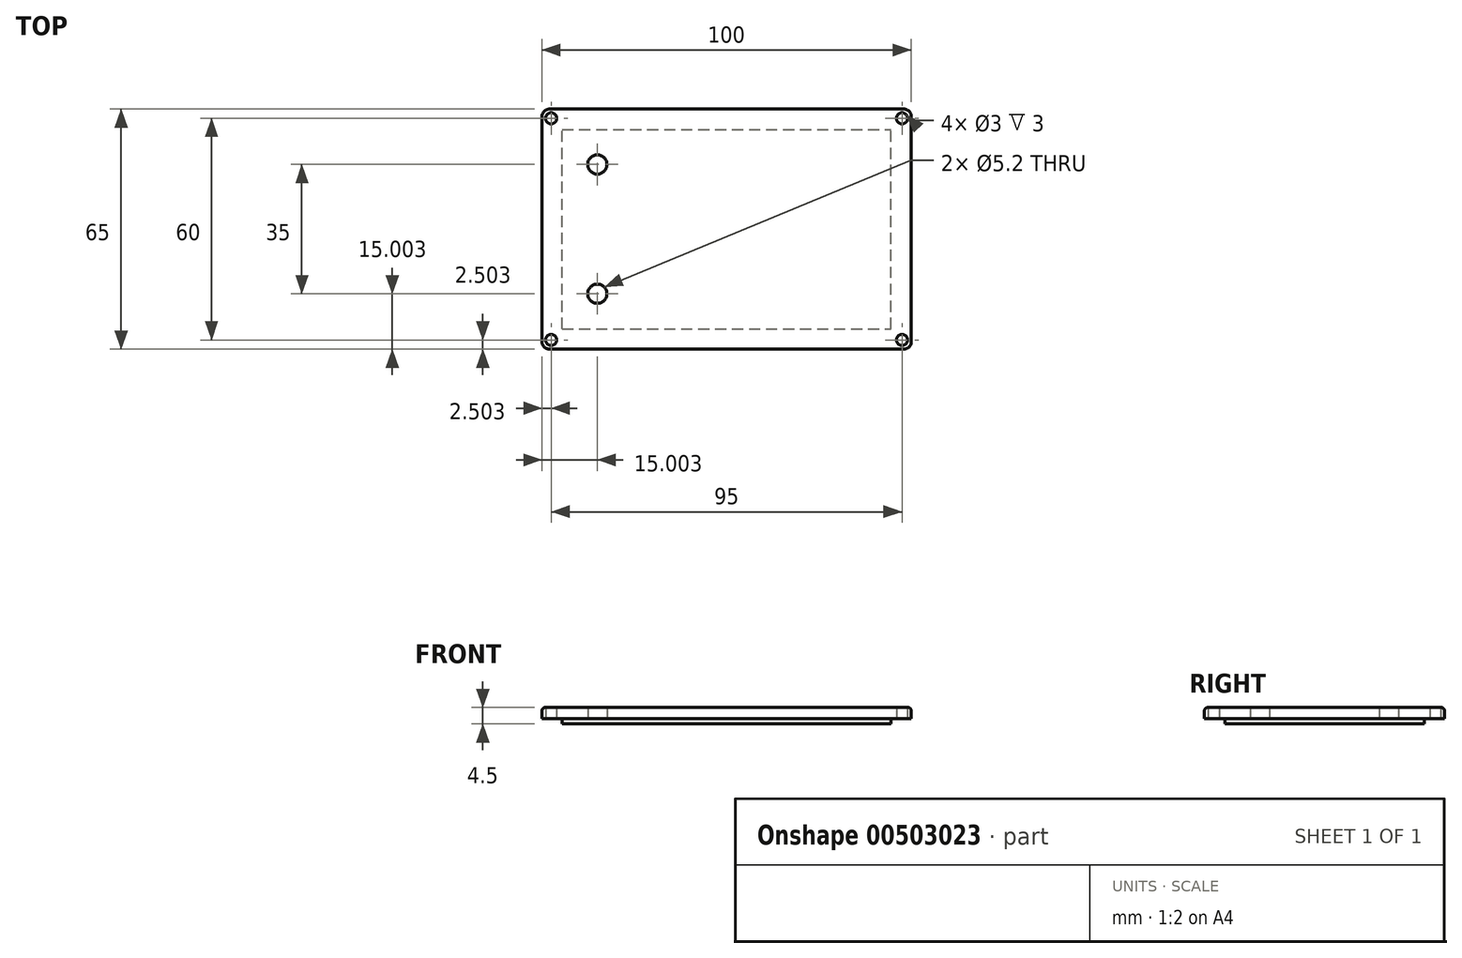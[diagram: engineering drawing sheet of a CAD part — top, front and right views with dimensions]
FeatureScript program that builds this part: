
annotation { "Feature Type Name" : "Feature", "Feature Type Description" : "" }
export const myFeature = defineFeature(function(context is Context, id is Id, definition is map)
    precondition{}
    {
        {
            var Q0;
            Q0=qCreatedBy(makeId("Top.planeOp"),FACE);
            var sketch = newSketch(context, id + "F0", { "sketchPlane" : qUnion([Q0])});
            skLineSegment(sketch, "E0.bottom", {"start": v(-45.15, 19.08) * mm, "end": v(54.85, 19.08) * mm});
            skLineSegment(sketch, "E0.top", {"start": v(-45.15, -45.92) * mm, "end": v(54.85, -45.92) * mm});
            skLineSegment(sketch, "E0.left", {"start": v(-45.15, 19.08) * mm, "end": v(-45.15, -45.92) * mm});
            skLineSegment(sketch, "E0.right", {"start": v(54.85, 19.08) * mm, "end": v(54.85, -45.92) * mm});
            skCircle(sketch, "E1", {"center": v(-42.65, 16.58) * mm, "radius": 1.5 * mm});
            skCircle(sketch, "E2", {"center": v(-42.65, -43.42) * mm, "radius": 1.5 * mm});
            skCircle(sketch, "E3", {"center": v(52.35, 16.58) * mm, "radius": 1.5 * mm});
            skCircle(sketch, "E4", {"center": v(52.35, -43.42) * mm, "radius": 1.5 * mm});
            skCircle(sketch, "E5", {"center": v(-30.15, 4.08) * mm, "radius": 2.6 * mm});
            skCircle(sketch, "E6", {"center": v(-30.15, -30.92) * mm, "radius": 2.6 * mm});
            skSolve(sketch);
        }
        {
            var Q0;
            Q0=makeQuery(id+"F0.imprint","IMPRINT",FACE,{"disambiguationData":[TD([[makeQuery(id+"F0.imprint","IMPRINT",EDGE,{"derivedFrom":sQuery(id+"F0.wireOp",EDGE,"E0.bottom")}),-1.0]])]});
            extrude(context, id + "F1", {"entities" : qUnion([Q0]), "depth" : 3 * mm});
        }
        {
            var Q0;
            Q0=makeQuery(id+"F1.opExtrude","CAP_EDGE",EDGE,{"disambiguationData":[OSD([sQuery(id+"F0.wireOp",EDGE,"E0.left")])],"isStart":false});
            var Q1;
            Q1=makeQuery(id+"F1.opExtrude","CAP_EDGE",EDGE,{"disambiguationData":[OSD([sQuery(id+"F0.wireOp",EDGE,"E0.bottom")])],"isStart":false});
            var Q2;
            Q2=makeQuery(id+"F1.opExtrude","CAP_EDGE",EDGE,{"disambiguationData":[OSD([sQuery(id+"F0.wireOp",EDGE,"E0.right")])],"isStart":false});
            var Q3;
            Q3=makeQuery(id+"F1.opExtrude","CAP_EDGE",EDGE,{"disambiguationData":[OSD([sQuery(id+"F0.wireOp",EDGE,"E0.top")])],"isStart":false});
            fillet(context, id + "F2", {"entities" : qUnion([Q0, Q1, Q2, Q3]), "radius" : 1 * mm, "tangentPropagation" : true, "allowEdgeOverflow" : false});
        }
        {
            var Q0;
            Q0=makeQuery(id+"F1.opExtrude","SWEPT_EDGE",EDGE,{"disambiguationData":[OSD([sQuery(id+"F0.wireOp",EDGE,"E0.top"),sQuery(id+"F0.wireOp",EDGE,"E0.left")])]});
            var Q1;
            Q1=makeQuery(id+"F1.opExtrude","SWEPT_EDGE",EDGE,{"disambiguationData":[OSD([sQuery(id+"F0.wireOp",EDGE,"E0.bottom"),sQuery(id+"F0.wireOp",EDGE,"E0.left")])]});
            var Q2;
            Q2=makeQuery(id+"F1.opExtrude","SWEPT_EDGE",EDGE,{"disambiguationData":[OSD([sQuery(id+"F0.wireOp",EDGE,"E0.bottom"),sQuery(id+"F0.wireOp",EDGE,"E0.right")])]});
            var Q3;
            Q3=makeQuery(id+"F1.opExtrude","SWEPT_EDGE",EDGE,{"disambiguationData":[OSD([sQuery(id+"F0.wireOp",EDGE,"E0.top"),sQuery(id+"F0.wireOp",EDGE,"E0.right")])]});
            fillet(context, id + "F3", {"entities" : qUnion([Q0, Q1, Q2, Q3]), "radius" : 2 * mm, "tangentPropagation" : true, "allowEdgeOverflow" : false});
        }
        {
            var Q0;
            Q0=makeQuery(id+"F1.opExtrude","CAP_FACE",FACE,{"disambiguationData":[OSD([sQuery(id+"F0.wireOp",EDGE,"E0.bottom"),sQuery(id+"F0.wireOp",EDGE,"E0.top"),sQuery(id+"F0.wireOp",EDGE,"E0.left"),sQuery(id+"F0.wireOp",EDGE,"E0.right"),sQuery(id+"F0.wireOp",EDGE,"E1"),sQuery(id+"F0.wireOp",EDGE,"E2"),sQuery(id+"F0.wireOp",EDGE,"E3"),sQuery(id+"F0.wireOp",EDGE,"E4"),sQuery(id+"F0.wireOp",EDGE,"E5"),sQuery(id+"F0.wireOp",EDGE,"E6")])],"isStart":true});
            var sketch = newSketch(context, id + "F4", { "sketchPlane" : qUnion([Q0])});
            skLineSegment(sketch, "E7.bottom", {"start": v(-39.65, 40.42) * mm, "end": v(49.35, 40.42) * mm});
            skLineSegment(sketch, "E7.top", {"start": v(-39.65, -13.58) * mm, "end": v(49.35, -13.58) * mm});
            skLineSegment(sketch, "E7.left", {"start": v(-39.65, 40.42) * mm, "end": v(-39.65, -13.58) * mm});
            skLineSegment(sketch, "E7.right", {"start": v(49.35, 40.42) * mm, "end": v(49.35, -13.58) * mm});
            skSolve(sketch);
        }
        {
            var Q0;
            Q0=makeQuery(id+"F4.imprint","IMPRINT",FACE,{"disambiguationData":[TD([[makeQuery(id+"F4.imprint","IMPRINT",EDGE,{"derivedFrom":sQuery(id+"F4.wireOp",EDGE,"E7.bottom")}),-1.0]])]});
            extrude(context, id + "F5", {"entities" : qUnion([Q0]), "operationType" : NewBodyOperationType.ADD, "depth" : 1.5 * mm});
        }
    });
